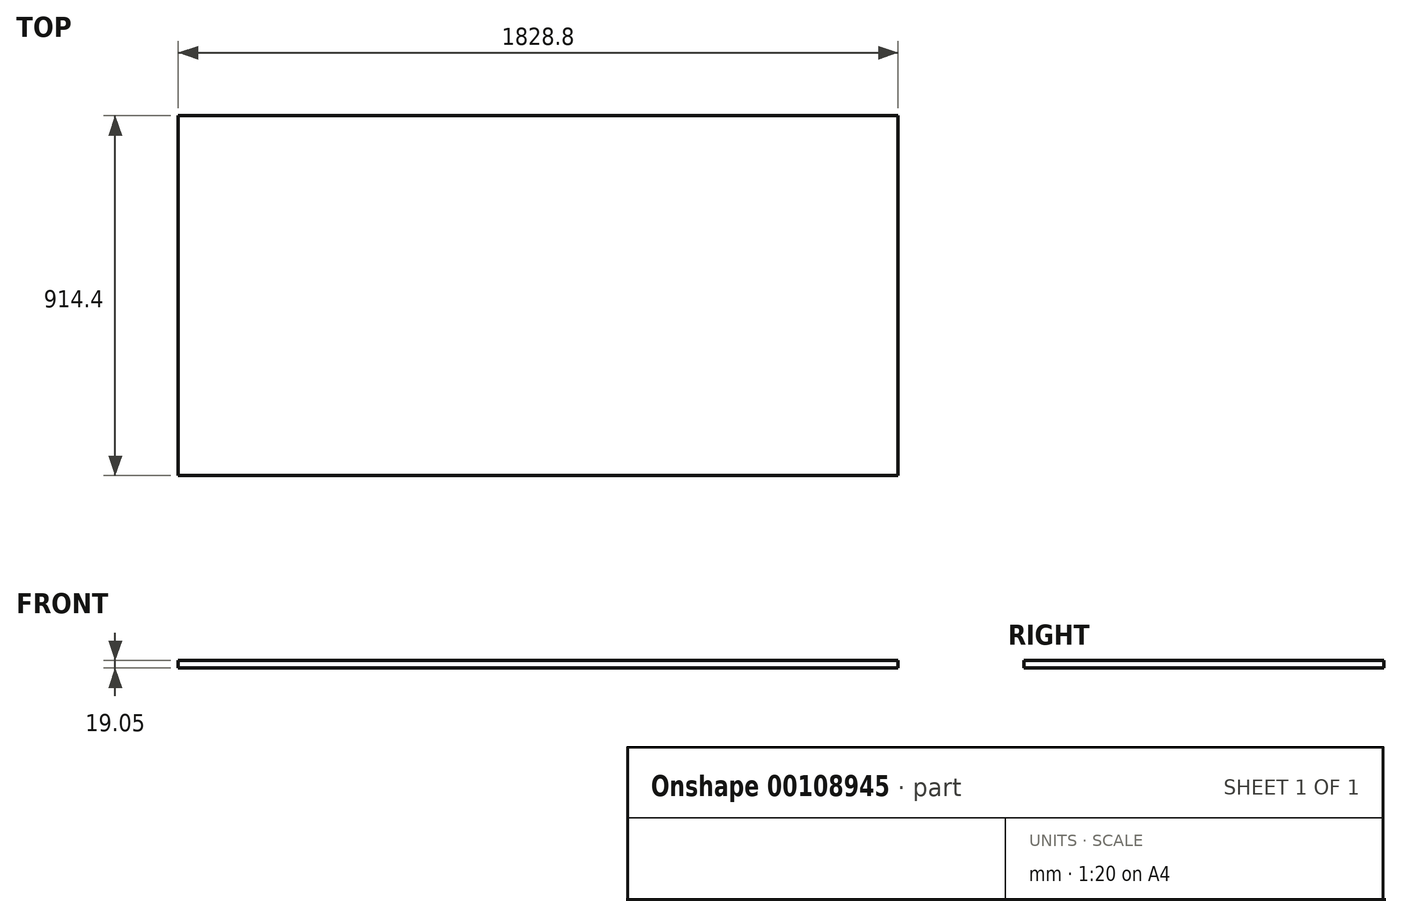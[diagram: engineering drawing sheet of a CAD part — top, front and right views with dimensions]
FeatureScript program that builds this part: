
annotation { "Feature Type Name" : "Feature", "Feature Type Description" : "" }
export const myFeature = defineFeature(function(context is Context, id is Id, definition is map)
    precondition{}
    {
        {
            var Q0;
            Q0=qCreatedBy(makeId("Top.planeOp"),FACE);
            var sketch = newSketch(context, id + "F0", { "sketchPlane" : qUnion([Q0])});
            skLineSegment(sketch, "E0.bottom", {"start": v(914.4, -457.2) * mm, "end": v(-914.4, -457.2) * mm});
            skLineSegment(sketch, "E0.top", {"start": v(914.4, 457.2) * mm, "end": v(-914.4, 457.2) * mm});
            skLineSegment(sketch, "E0.left", {"start": v(914.4, -457.2) * mm, "end": v(914.4, 457.2) * mm});
            skLineSegment(sketch, "E0.right", {"start": v(-914.4, -457.2) * mm, "end": v(-914.4, 457.2) * mm});
            skPoint(sketch, "E0.middle", {"position": v(0, 0) * mm});
            skSolve(sketch);
        }
        {
            var Q0;
            Q0=makeQuery(id+"F0.imprint","IMPRINT",FACE,{"disambiguationData":[TD([[makeQuery(id+"F0.imprint","IMPRINT",EDGE,{"derivedFrom":sQuery(id+"F0.wireOp",EDGE,"E0.bottom")}),-1.0]])]});
            extrude(context, id + "F1", {"entities" : qUnion([Q0]), "depth" : 19.05 * mm});
        }
    });
